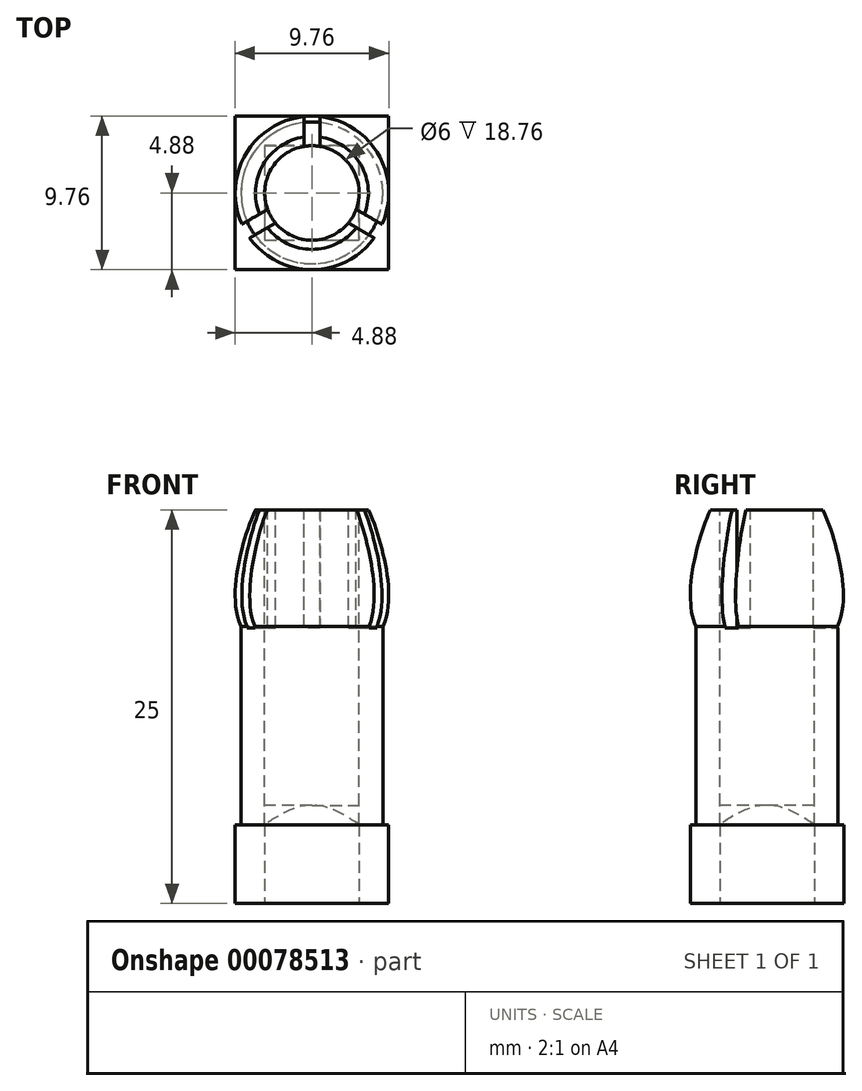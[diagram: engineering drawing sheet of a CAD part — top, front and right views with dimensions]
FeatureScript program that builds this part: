
annotation { "Feature Type Name" : "Feature", "Feature Type Description" : "" }
export const myFeature = defineFeature(function(context is Context, id is Id, definition is map)
    precondition{}
    {
        {
            var Q0;
            Q0=qCreatedBy(makeId("Top.planeOp"),FACE);
            var sketch = newSketch(context, id + "F0", { "sketchPlane" : qUnion([Q0])});
            skLineSegment(sketch, "E0.bottom", {"start": v(-4.88, 4.88) * mm, "end": v(4.88, 4.88) * mm});
            skLineSegment(sketch, "E0.top", {"start": v(-4.88, -4.87) * mm, "end": v(4.88, -4.88) * mm});
            skLineSegment(sketch, "E0.left", {"start": v(-4.87, 4.87) * mm, "end": v(-4.88, -4.88) * mm});
            skLineSegment(sketch, "E0.right", {"start": v(4.88, 4.88) * mm, "end": v(4.87, -4.87) * mm});
            skPoint(sketch, "E1", {"position": v(4.88, 0) * mm});
            skPoint(sketch, "E2", {"position": v(0, 4.88) * mm});
            skLineSegment(sketch, "E3.bottom", {"start": v(-3, 3) * mm, "end": v(3, 3) * mm});
            skLineSegment(sketch, "E3.top", {"start": v(-3, -3) * mm, "end": v(3, -3) * mm});
            skLineSegment(sketch, "E3.left", {"start": v(-3, 3) * mm, "end": v(-3, -3) * mm});
            skLineSegment(sketch, "E3.right", {"start": v(3, 3) * mm, "end": v(3, -3) * mm});
            skPoint(sketch, "E4", {"position": v(0, 3) * mm});
            skPoint(sketch, "E5", {"position": v(3, 0) * mm});
            skSolve(sketch);
        }
        {
            var Q0;
            Q0=makeQuery(id+"F0.imprint","IMPRINT",FACE,{"disambiguationData":[TD([[makeQuery(id+"F0.imprint","IMPRINT",EDGE,{"derivedFrom":sQuery(id+"F0.wireOp",EDGE,"E0.bottom")}),-1.0]])]});
            extrude(context, id + "F1", {"entities" : qUnion([Q0]), "depth" : 5 * mm});
        }
        {
            var Q0;
            Q0=qCreatedBy(makeId("Front.planeOp"),FACE);
            var sketch = newSketch(context, id + "F2", { "sketchPlane" : qUnion([Q0])});
            skLineSegment(sketch, "E6", {"start": v(0, 17.75) * mm, "end": v(0, -7.74) * mm});
            skLineSegment(sketch, "E7.0", {"start": v(-4.88, 5) * mm, "end": v(4.87, 5) * mm});
            skLineSegment(sketch, "E8", {"start": v(3, 5) * mm, "end": v(3, 25) * mm});
            skLineSegment(sketch, "E9", {"start": v(3, 25) * mm, "end": v(3.58, 25) * mm});
            skLineSegment(sketch, "E10", {"start": v(4.5, 5) * mm, "end": v(4.5, 17.6) * mm});
            skFitSpline(sketch, "E11", {"points": [v(3.58, 25) * mm, v(4.5, 17.6) * mm], "startDerivative": vector(1.55, -3.12) * mm, "endDerivative": vector(-3.16, -6.4) * mm});
            skLineSegment(sketch, "E12", {"start": v(4.87, 5) * mm, "end": v(4.87, 17.4) * mm, "construction": true});
            skSolve(sketch);
        }
        {
            var Q0;
            {var subQ1=sQuery(id+"F2.wireOp",EDGE,"E8");Q0=makeQuery(id+"F2.imprint","IMPRINT",FACE,{"disambiguationData":[TD([[makeQuery(id+"F2.imprint","IMPRINT",EDGE,{"derivedFrom":subQ1}),-1.0]])]});}
            var Q1;
            Q1=sQuery(id+"F2.wireOp",EDGE,"E6");
            revolve(context, id + "F3", {"operationType" : NewBodyOperationType.ADD, "entities" : qUnion([Q0]), "axis" : qUnion([Q1]), "revolveType" : RevolveType.FULL});
        }
        {
            var Q0;
            Q0=makeQuery(id+"F3.opRevolve","SWEPT_FACE",FACE,{"disambiguationData":[OSD([sQuery(id+"F2.wireOp",EDGE,"E9")])]});
            var sketch = newSketch(context, id + "F4", { "sketchPlane" : qUnion([Q0])});
            skCircle(sketch, "E13.cCircle", {"center": v(0, 0) * mm, "radius": 3.91 * mm, "construction": true});
            skLineSegment(sketch, "E13.0", {"start": v(0, 7.83) * mm, "end": v(6.78, -3.91) * mm, "construction": true});
            skLineSegment(sketch, "E13.1", {"start": v(6.78, -3.91) * mm, "end": v(-6.78, -3.91) * mm, "construction": true});
            skLineSegment(sketch, "E13.2", {"start": v(-6.78, -3.91) * mm, "end": v(0, 7.83) * mm, "construction": true});
            skPoint(sketch, "E13.0.midPoint", {"position": v(3.4, 1.96) * mm});
            skLineSegment(sketch, "E14", {"start": v(0, 0) * mm, "end": v(0, 7.83) * mm, "construction": true});
            skLineSegment(sketch, "E15", {"start": v(0, 0) * mm, "end": v(6.78, -3.91) * mm, "construction": true});
            skLineSegment(sketch, "E16", {"start": v(0, 0) * mm, "end": v(-6.78, -3.91) * mm, "construction": true});
            skLineSegment(sketch, "E17", {"start": v(-0.5, 10.77) * mm, "end": v(-0.5, 0.29) * mm});
            skLineSegment(sketch, "E18", {"start": v(-0.5, 0.29) * mm, "end": v(0.5, 0.29) * mm});
            skLineSegment(sketch, "E19", {"start": v(0.5, 0.29) * mm, "end": v(0.5, 10.77) * mm});
            skLineSegment(sketch, "E20", {"start": v(0.5, 10.77) * mm, "end": v(-0.5, 10.77) * mm});
            skLineSegment(sketch, "E21", {"start": v(0.5, 0.29) * mm, "end": v(9.57, -4.95) * mm});
            skLineSegment(sketch, "E22", {"start": v(9.57, -4.95) * mm, "end": v(9.07, -5.82) * mm});
            skLineSegment(sketch, "E23", {"start": v(9.07, -5.82) * mm, "end": v(0, -0.58) * mm});
            skLineSegment(sketch, "E24", {"start": v(0, -0.58) * mm, "end": v(0.5, 0.29) * mm});
            skPoint(sketch, "E25", {"position": v(0, 10.77) * mm});
            skPoint(sketch, "E26", {"position": v(0.25, -0.14) * mm});
            skLineSegment(sketch, "E27", {"start": v(-0.5, 0.29) * mm, "end": v(-9.57, -4.95) * mm});
            skLineSegment(sketch, "E28", {"start": v(-9.57, -4.95) * mm, "end": v(-9.07, -5.82) * mm});
            skLineSegment(sketch, "E29", {"start": v(-9.07, -5.82) * mm, "end": v(0, -0.58) * mm});
            skLineSegment(sketch, "E30", {"start": v(0, -0.58) * mm, "end": v(-0.5, 0.29) * mm});
            skPoint(sketch, "E31", {"position": v(-9.32, -5.38) * mm});
            skSolve(sketch);
        }
        {
            var Q0;
            Q0 = qSketchRegion(id + "F4", true);
            extrude(context, id + "F5", {"entities" : qUnion([Q0]), "operationType" : NewBodyOperationType.REMOVE, "oppositeDirection" : true, "depth" : 7.5 * mm});
        }
        {
            var Q0;
            {var subQ0=sQuery(id+"F2.wireOp",EDGE,"E7.0");var subQ1=sQuery(id+"F2.wireOp",EDGE,"E8");Q0=makeQuery(id+"F3.boolean.opBoolean","SPLIT",EDGE,{"disambiguationData":[TD([makeQuery(id+"F1.opExtrude","SWEPT_FACE",FACE,{"disambiguationData":[OSD([sQuery(id+"F0.wireOp",EDGE,"E3.top")])]}),makeQuery(id+"F1.opExtrude","SWEPT_FACE",FACE,{"disambiguationData":[OSD([sQuery(id+"F0.wireOp",EDGE,"E3.left")])]}),makeQuery(id+"F3.opRevolve","SWEPT_FACE",FACE,{"disambiguationData":[OSD([subQ0])]}),makeQuery(id+"F3.opRevolve","SWEPT_FACE",FACE,{"disambiguationData":[OSD([subQ1])]})])],"derivedFrom":makeQuery(id+"F3.opRevolve","SWEPT_EDGE",EDGE,{"disambiguationData":[OSD([subQ0,subQ1])]})});}
            chamfer(context, id + "F6", {"entities" : qUnion([Q0]), "width" : 1.24 * mm, "tangentPropagation" : true});
        }
    });
